# Revit family: 540_Sliding_Window_XOX_Standard
name_source: partatom
category: Windows
revit_build: Autodesk Revit 2014 (Build: 20130308_1515(x64)
units: mm (PartAtom-declared; Revit-internal decimal feet)

## types (96) — shared parameters
Centered In Wall = Yes
Custom Sash Width Middle = 800 mm  [stored 2.62467 ft]
Default Sill Height = 800 mm  [stored 2.62467 ft]
Description = Sliding window, XOX
Equal Sash Width = Yes
Frame Thickness = 54 mm  [stored 0.177165 ft]
Limit Sash Height Max = 1500 mm  [stored 4.92126 ft]
Limit Sash Height Min = 300 mm  [stored 0.984252 ft]
Limit Sash Width Max = 1200 mm  [stored 3.93701 ft]
Limit Sash Width Min = 300 mm  [stored 0.984252 ft]
Limit Window Height Max = 1580 mm
Limit Window Height Min = 380 mm
Limit Window Width Max = 3556 mm
Limit Window Width Min = 856 mm
Manufacturer = Crealco
Model = 540
Sash Frame Seal = 3 mm  [stored 0.00984252 ft]
URL = http://www.crealco.co.za
Wall Closure = By host
zero-valued in all types: Custom Frame Offset From Exterior

## per-type parameters (varying)
| type | Area Middle Sash Glazing | Area Side Sash Glazing | Clearvue SHGC Value | Clearvue U Value | Custom Windload | Custom Window Height | Custom Window Width | Energy Advantage SHGC Value | Heavy Duty Interlocker | Height | Intruderprufe LowE SHGC Value | Intruderprufe LowE U Value | Intruderprufe SHGC Value | Intruderprufe U Value | Is Heavy Duty Mullion | Limit Sash Width Middle Max | Limit Sash Width Middle Min | Max Pane Area | Sash Height | Sash Width Middle | Sash Width Sides | Standard Interlocker | Width | Windload Design |
| 540SW-0906XOX-1000Pa | 0.08 m² | 0.08 m² | 0.327 | 6.76 | 1000 mm  [stored 3.28084 ft] | 590 mm  [stored 1.9357 ft] | 890 mm  [stored 2.91995 ft] | 0.327 | No | 590 mm  [stored 1.9357 ft] | 0.306 | 6.65 | 0.34 | 7.43 | 0 mm  [stored 0 ft] | 334 mm | 300 mm  [stored 0.984252 ft] | 0.08 m² | 510 mm | 311 mm | 311 mm | Yes | 890 mm  [stored 2.91995 ft] | 1000 mm  [stored 3.28084 ft] |
| 540SW-1206XOX-1000Pa | 0.12 m² | 0.12 m² | 0.409 | 7.29 | 1000 mm  [stored 3.28084 ft] | 590 mm  [stored 1.9357 ft] | 1190 mm  [stored 3.9042 ft] | 0.371 | No | 590 mm  [stored 1.9357 ft] | 0.347 | 6.27 | 0.388 | 7.148 | 0 mm  [stored 0 ft] | 634 mm | 300 mm  [stored 0.984252 ft] | 0.12 m² | 510 mm | 411 mm | 411 mm | Yes | 1190 mm  [stored 3.9042 ft] | 1000 mm  [stored 3.28084 ft] |
| 540SW-1506XOX-1000Pa | 0.16 m² | 0.16 m² | 0.44 | 7.15 | 1000 mm  [stored 3.28084 ft] | 590 mm  [stored 1.9357 ft] | 1490 mm  [stored 4.88845 ft] | 0.398 | No | 590 mm  [stored 1.9357 ft] | 0.372 | 6.03 | 0.416 | 7.03 | 0 mm  [stored 0 ft] | 934 mm | 300 mm  [stored 0.984252 ft] | 0.16 m² | 510 mm | 511 mm | 511 mm | Yes | 1490 mm  [stored 4.88845 ft] | 1000 mm  [stored 3.28084 ft] |
| 540SW-1806XOX-1000Pa | 0.2 m² | 0.2 m² | 0.46 | 7.26 | 1000 mm  [stored 3.28084 ft] | 590 mm  [stored 1.9357 ft] | 1790 mm  [stored 5.8727 ft] | 0.415 | No | 590 mm  [stored 1.9357 ft] | 0.389 | 6.01 | 0.435 | 7.1 | 0 mm  [stored 0 ft] | 1200 mm  [stored 3.93701 ft] | 300 mm  [stored 0.984252 ft] | 0.2 m² | 510 mm | 611 mm | 611 mm | Yes | 1790 mm  [stored 5.8727 ft] | 1000 mm  [stored 3.28084 ft] |
| 540SW-2106XOX-1000Pa | 0.24 m² | 0.24 m² | 0.475 | 7.16 | 1000 mm  [stored 3.28084 ft] | 590 mm  [stored 1.9357 ft] | 2090 mm  [stored 6.85696 ft] | 0.428 | No | 590 mm  [stored 1.9357 ft] | 0.4 | 5.88 | 0.449 | 7 | 0 mm  [stored 0 ft] | 1200 mm  [stored 3.93701 ft] | 300 mm  [stored 0.984252 ft] | 0.24 m² | 510 mm | 711 mm | 711 mm | Yes | 2090 mm  [stored 6.85696 ft] | 1000 mm  [stored 3.28084 ft] |
| 540SW-2706XOX-1000Pa | 0.32 m² | 0.32 m² | 0.494 | 7.03 | 1000 mm  [stored 3.28084 ft] | 590 mm  [stored 1.9357 ft] | 2690 mm | 0.445 | No | 590 mm  [stored 1.9357 ft] | 0.416 | 5.71 | 0.467 | 6.88 | 0 mm  [stored 0 ft] | 1200 mm  [stored 3.93701 ft] | 334 mm | 0.32 m² | 510 mm | 911 mm | 911 mm | Yes | 2690 mm | 1000 mm  [stored 3.28084 ft] |
| 540SW-3006XOX-1000Pa | 0.36 m² | 0.36 m² | 0.501 | 6.98 | 1000 mm  [stored 3.28084 ft] | 590 mm  [stored 1.9357 ft] | 2990 mm  [stored 9.80971 ft] | 0.45 | No | 590 mm  [stored 1.9357 ft] | 0.421 | 5.65 | 0.473 | 6.84 | 0 mm  [stored 0 ft] | 1200 mm  [stored 3.93701 ft] | 634 mm | 0.36 m² | 510 mm | 1011 mm | 1011 mm | Yes | 2990 mm  [stored 9.80971 ft] | 1000 mm  [stored 3.28084 ft] |
| 540SW-0909XOX-1000Pa | 0.14 m² | 0.14 m² | 0.417 | 7.52 | 1000 mm  [stored 3.28084 ft] | 890 mm  [stored 2.91995 ft] | 890 mm  [stored 2.91995 ft] | 0.378 | No | 890 mm  [stored 2.91995 ft] | 0.353 | 6.47 | 0.394 | 7.4 | 0 mm  [stored 0 ft] | 334 mm | 300 mm  [stored 0.984252 ft] | 0.14 m² | 810 mm  [stored 2.65748 ft] | 311 mm | 311 mm | Yes | 890 mm  [stored 2.91995 ft] | 1000 mm  [stored 3.28084 ft] |
| 540SW-1209XOX-1000Pa | 0.21 m² | 0.21 m² | 0.477 | 7.22 | 1000 mm  [stored 3.28084 ft] | 890 mm  [stored 2.91995 ft] | 1190 mm  [stored 3.9042 ft] | 0.431 | No | 890 mm  [stored 2.91995 ft] | 0.402 | 6.01 | 0.451 | 7.11 | 0 mm  [stored 0 ft] | 634 mm | 300 mm  [stored 0.984252 ft] | 0.21 m² | 810 mm  [stored 2.65748 ft] | 411 mm | 411 mm | Yes | 1190 mm  [stored 3.9042 ft] | 1000 mm  [stored 3.28084 ft] |
| 540SW-1509XOX-1000Pa | 0.28 m² | 0.28 m² | 0.513 | 7.04 | 1000 mm  [stored 3.28084 ft] | 890 mm  [stored 2.91995 ft] | 1490 mm  [stored 4.88845 ft] | 0.463 | No | 890 mm  [stored 2.91995 ft] | 0.432 | 5.73 | 0.485 | 6.93 | 0 mm  [stored 0 ft] | 934 mm | 300 mm  [stored 0.984252 ft] | 0.28 m² | 810 mm  [stored 2.65748 ft] | 511 mm | 511 mm | Yes | 1490 mm  [stored 4.88845 ft] | 1000 mm  [stored 3.28084 ft] |
| 540SW-1809XOX-1000Pa | 0.35 m² | 0.35 m² | 0.538 | 7.15 | 1000 mm  [stored 3.28084 ft] | 890 mm  [stored 2.91995 ft] | 1790 mm  [stored 5.8727 ft] | 0.483 | No | 890 mm  [stored 2.91995 ft] | 0.452 | 5.68 | 0.508 | 6.98 | 0 mm  [stored 0 ft] | 1200 mm  [stored 3.93701 ft] | 300 mm  [stored 0.984252 ft] | 0.35 m² | 810 mm  [stored 2.65748 ft] | 611 mm | 611 mm | Yes | 1790 mm  [stored 5.8727 ft] | 1000 mm  [stored 3.28084 ft] |
| 540SW-2109XOX-1000Pa | 0.42 m² | 0.42 m² | 0.555 | 7.04 | 1000 mm  [stored 3.28084 ft] | 890 mm  [stored 2.91995 ft] | 2090 mm  [stored 6.85696 ft] | 0.499 | No | 890 mm  [stored 2.91995 ft] | 0.466 | 5.52 | 0.524 | 6.87 | 0 mm  [stored 0 ft] | 1200 mm  [stored 3.93701 ft] | 300 mm  [stored 0.984252 ft] | 0.42 m² | 810 mm  [stored 2.65748 ft] | 711 mm | 711 mm | Yes | 2090 mm  [stored 6.85696 ft] | 1000 mm  [stored 3.28084 ft] |
| 540SW-2409XOX-1000Pa | 0.49 m² | 0.49 m² | 0.568 | 6.95 | 1000 mm  [stored 3.28084 ft] | 890 mm  [stored 2.91995 ft] | 2390 mm  [stored 7.84121 ft] | 0.51 | No | 890 mm  [stored 2.91995 ft] | 0.476 | 5.41 | 0.536 | 6.79 | 0 mm  [stored 0 ft] | 1200 mm  [stored 3.93701 ft] | 300 mm  [stored 0.984252 ft] | 0.49 m² | 810 mm  [stored 2.65748 ft] | 811 mm | 811 mm | Yes | 2390 mm  [stored 7.84121 ft] | 1000 mm  [stored 3.28084 ft] |
| 540SW-2709XOX-1000Pa | 0.56 m² | 0.56 m² | 0.578 | 6.88 | 1000 mm  [stored 3.28084 ft] | 890 mm  [stored 2.91995 ft] | 2690 mm | 0.519 | No | 890 mm  [stored 2.91995 ft] | 0.484 | 5.32 | 0.546 | 6.72 | 0 mm  [stored 0 ft] | 1200 mm  [stored 3.93701 ft] | 334 mm | 0.56 m² | 810 mm  [stored 2.65748 ft] | 911 mm | 911 mm | Yes | 2690 mm | 1000 mm  [stored 3.28084 ft] |
| 540SW-3009XOX-1000Pa | 0.63 m² | 0.63 m² | 0.586 | 6.82 | 1000 mm  [stored 3.28084 ft] | 890 mm  [stored 2.91995 ft] | 2990 mm  [stored 9.80971 ft] | 0.526 | No | 890 mm  [stored 2.91995 ft] | 0.491 | 5.25 | 0.553 | 6.69 | 0 mm  [stored 0 ft] | 1200 mm  [stored 3.93701 ft] | 634 mm | 0.63 m² | 810 mm  [stored 2.65748 ft] | 1011 mm | 1011 mm | Yes | 2990 mm  [stored 9.80971 ft] | 1000 mm  [stored 3.28084 ft] |
| 540SW-0912XOX-1000Pa | 0.2 m² | 0.2 m² | 0.445 | 7.51 | 1000 mm  [stored 3.28084 ft] | 1190 mm  [stored 3.9042 ft] | 890 mm  [stored 2.91995 ft] | 0.403 | No | 1190 mm  [stored 3.9042 ft] | 0.377 | 6.38 | 0.421 | 7.39 | 0 mm  [stored 0 ft] | 334 mm | 300 mm  [stored 0.984252 ft] | 0.2 m² | 1110 mm  [stored 3.64173 ft] | 311 mm | 311 mm | Yes | 890 mm  [stored 2.91995 ft] | 1000 mm  [stored 3.28084 ft] |
| 540SW-1212XOX-1000Pa | 0.3 m² | 0.3 m² | 0.511 | 7.19 | 1000 mm  [stored 3.28084 ft] | 1190 mm  [stored 3.9042 ft] | 1190 mm  [stored 3.9042 ft] | 0.461 | No | 1190 mm  [stored 3.9042 ft] | 0.43 | 5.88 | 0.482 | 7.07 | 0 mm  [stored 0 ft] | 634 mm | 300 mm  [stored 0.984252 ft] | 0.3 m² | 1110 mm  [stored 3.64173 ft] | 411 mm | 411 mm | Yes | 1190 mm  [stored 3.9042 ft] | 1000 mm  [stored 3.28084 ft] |
| 540SW-1512XOX-1000Pa | 0.4 m² | 0.4 m² | 0.55 | 6.99 | 1000 mm  [stored 3.28084 ft] | 1190 mm  [stored 3.9042 ft] | 1490 mm  [stored 4.88845 ft] | 0.495 | No | 1190 mm  [stored 3.9042 ft] | 0.462 | 5.57 | 0.519 | 6.87 | 0 mm  [stored 0 ft] | 934 mm | 300 mm  [stored 0.984252 ft] | 0.4 m² | 1110 mm  [stored 3.64173 ft] | 511 mm | 511 mm | Yes | 1490 mm  [stored 4.88845 ft] | 1000 mm  [stored 3.28084 ft] |
| 540SW-1812XOX-1000Pa | 0.5 m² | 0.5 m² | 0.576 | 7.1 | 1000 mm  [stored 3.28084 ft] | 1190 mm  [stored 3.9042 ft] | 1790 mm  [stored 5.8727 ft] | 0.517 | No | 1190 mm  [stored 3.9042 ft] | 0.483 | 5.52 | 0.544 | 6.92 | 0 mm  [stored 0 ft] | 1200 mm  [stored 3.93701 ft] | 300 mm  [stored 0.984252 ft] | 0.5 m² | 1110 mm  [stored 3.64173 ft] | 611 mm | 611 mm | Yes | 1790 mm  [stored 5.8727 ft] | 1000 mm  [stored 3.28084 ft] |
| 540SW-2112XOX-1000Pa | 0.6 m² | 0.6 m² | 0.595 | 6.98 | 1000 mm  [stored 3.28084 ft] | 1190 mm  [stored 3.9042 ft] | 2090 mm  [stored 6.85696 ft] | 0.534 | No | 1190 mm  [stored 3.9042 ft] | 0.498 | 5.35 | 0.561 | 6.8 | 0 mm  [stored 0 ft] | 1200 mm  [stored 3.93701 ft] | 300 mm  [stored 0.984252 ft] | 0.6 m² | 1110 mm  [stored 3.64173 ft] | 711 mm | 711 mm | Yes | 2090 mm  [stored 6.85696 ft] | 1000 mm  [stored 3.28084 ft] |
| 540SW-2412XOX-1000Pa | 0.71 m² | 0.71 m² | 0.609 | 6.88 | 1000 mm  [stored 3.28084 ft] | 1190 mm  [stored 3.9042 ft] | 2390 mm  [stored 7.84121 ft] | 0.546 | No | 1190 mm  [stored 3.9042 ft] | 0.51 | 5.23 | 0.575 | 6.72 | 0 mm  [stored 0 ft] | 1200 mm  [stored 3.93701 ft] | 300 mm  [stored 0.984252 ft] | 0.71 m² | 1110 mm  [stored 3.64173 ft] | 811 mm | 811 mm | Yes | 2390 mm  [stored 7.84121 ft] | 1000 mm  [stored 3.28084 ft] |
| 540SW-2712XOX-1000Pa | 0.81 m² | 0.81 m² | 0.62 | 6.81 | 1000 mm  [stored 3.28084 ft] | 1190 mm  [stored 3.9042 ft] | 2690 mm | 0.556 | No | 1190 mm  [stored 3.9042 ft] | 0.518 | 5.13 | 0.585 | 6.65 | 0 mm  [stored 0 ft] | 1200 mm  [stored 3.93701 ft] | 334 mm | 0.81 m² | 1110 mm  [stored 3.64173 ft] | 911 mm | 911 mm | Yes | 2690 mm | 1000 mm  [stored 3.28084 ft] |
| 540SW-3012XOX-1000Pa | 0.91 m² | 0.91 m² | 0.629 | 6.75 | 1000 mm  [stored 3.28084 ft] | 1190 mm  [stored 3.9042 ft] | 2990 mm  [stored 9.80971 ft] | 0.563 | No | 1190 mm  [stored 3.9042 ft] | 0.525 | 5.05 | 0.593 | 6.59 | 0 mm  [stored 0 ft] | 1200 mm  [stored 3.93701 ft] | 634 mm | 0.91 m² | 1110 mm  [stored 3.64173 ft] | 1011 mm | 1011 mm | Yes | 2990 mm  [stored 9.80971 ft] | 1000 mm  [stored 3.28084 ft] |
| 540SW-0915XOX-1000Pa | 0.26 m² | 0.26 m² | 0.462 | 7.5 | 1000 mm  [stored 3.28084 ft] | 1490 mm  [stored 4.88845 ft] | 890 mm  [stored 2.91995 ft] | 0.419 | No | 1490 mm  [stored 4.88845 ft] | 0.391 | 6.33 | 0.437 | 7.38 | 0 mm  [stored 0 ft] | 334 mm | 300 mm  [stored 0.984252 ft] | 0.26 m² | 1410 mm | 311 mm | 311 mm | Yes | 890 mm  [stored 2.91995 ft] | 1000 mm  [stored 3.28084 ft] |
| 540SW-1215XOX-1000Pa | 0.4 m² | 0.4 m² | 0.531 | 7.17 | 1000 mm  [stored 3.28084 ft] | 1490 mm  [stored 4.88845 ft] | 1190 mm  [stored 3.9042 ft] | 0.478 | No | 1490 mm  [stored 4.88845 ft] | 0.446 | 5.8 | 0.501 | 7.05 | 0 mm  [stored 0 ft] | 634 mm | 300 mm  [stored 0.984252 ft] | 0.4 m² | 1410 mm | 411 mm | 411 mm | Yes | 1190 mm  [stored 3.9042 ft] | 1000 mm  [stored 3.28084 ft] |
| 540SW-1515XOX-1000Pa | 0.53 m² | 0.53 m² | 0.572 | 7.26 | 1000 mm  [stored 3.28084 ft] | 1490 mm  [stored 4.88845 ft] | 1490 mm  [stored 4.88845 ft] | 0.513 | No | 1490 mm  [stored 4.88845 ft] | 0.479 | 5.66 | 0.54 | 7.06 | 0 mm  [stored 0 ft] | 934 mm | 300 mm  [stored 0.984252 ft] | 0.53 m² | 1410 mm | 511 mm | 511 mm | Yes | 1490 mm  [stored 4.88845 ft] | 1000 mm  [stored 3.28084 ft] |
| 540SW-1815XOX-1000Pa | 0.66 m² | 0.66 m² | 0.599 | 7.07 | 1000 mm  [stored 3.28084 ft] | 1490 mm  [stored 4.88845 ft] | 1790 mm  [stored 5.8727 ft] | 0.538 | No | 1490 mm  [stored 4.88845 ft] | 0.502 | 5.42 | 0.565 | 6.89 | 0 mm  [stored 0 ft] | 1200 mm  [stored 3.93701 ft] | 300 mm  [stored 0.984252 ft] | 0.66 m² | 1410 mm | 611 mm | 611 mm | Yes | 1790 mm  [stored 5.8727 ft] | 1000 mm  [stored 3.28084 ft] |
| 540SW-2115XOX-1000Pa | 0.79 m² | 0.79 m² | 0.619 | 6.94 | 1000 mm  [stored 3.28084 ft] | 1490 mm  [stored 4.88845 ft] | 2090 mm  [stored 6.85696 ft] | 0.555 | Yes | 1490 mm  [stored 4.88845 ft] | 0.518 | 5.24 | 0.584 | 6.76 | 1 mm  [stored 0.00328084 ft] | 1200 mm  [stored 3.93701 ft] | 300 mm  [stored 0.984252 ft] | 0.79 m² | 1410 mm | 711 mm | 711 mm | No | 2090 mm  [stored 6.85696 ft] | 1000 mm  [stored 3.28084 ft] |
| 540SW-2415XOX-1000Pa | 0.92 m² | 0.92 m² | 0.633 | 6.84 | 1000 mm  [stored 3.28084 ft] | 1490 mm  [stored 4.88845 ft] | 2390 mm  [stored 7.84121 ft] | 0.568 | Yes | 1490 mm  [stored 4.88845 ft] | 0.529 | 5.12 | 0.597 | 6.67 | 1 mm  [stored 0.00328084 ft] | 1200 mm  [stored 3.93701 ft] | 300 mm  [stored 0.984252 ft] | 0.92 m² | 1410 mm | 811 mm | 811 mm | No | 2390 mm  [stored 7.84121 ft] | 1000 mm  [stored 3.28084 ft] |
| 540SW-2715XOX-1000Pa | 1.05 m² | 1.05 m² | 0.645 | 6.76 | 1000 mm  [stored 3.28084 ft] | 1490 mm  [stored 4.88845 ft] | 2690 mm | 0.578 | Yes | 1490 mm  [stored 4.88845 ft] | 0.539 | 5.02 | 0.608 | 6.6 | 1 mm  [stored 0.00328084 ft] | 1200 mm  [stored 3.93701 ft] | 334 mm | 1.05 m² | 1410 mm | 911 mm | 911 mm | No | 2690 mm | 1000 mm  [stored 3.28084 ft] |
| 540SW-3015XOX-1000Pa | 1.18 m² | 1.18 m² | 0.654 | 6.7 | 1000 mm  [stored 3.28084 ft] | 1490 mm  [stored 4.88845 ft] | 2990 mm  [stored 9.80971 ft] | 0.586 | Yes | 1490 mm  [stored 4.88845 ft] | 0.546 | 4.93 | 0.617 | 6.54 | 1 mm  [stored 0.00328084 ft] | 1200 mm  [stored 3.93701 ft] | 634 mm | 1.18 m² | 1410 mm | 1011 mm | 1011 mm | No | 2990 mm  [stored 9.80971 ft] | 1000 mm  [stored 3.28084 ft] |
| 540SW-2406XOX-1000Pa | 0.28 m² | 0.28 m² | 0.486 | 7.08 | 1000 mm  [stored 3.28084 ft] | 590 mm  [stored 1.9357 ft] | 2390 mm  [stored 7.84121 ft] | 0.437 | No | 590 mm  [stored 1.9357 ft] | 0.409 | 5.78 | 0.459 | 6.93 | 0 mm  [stored 0 ft] | 1200 mm  [stored 3.93701 ft] | 300 mm  [stored 0.984252 ft] | 0.28 m² | 510 mm | 811 mm | 811 mm | Yes | 2390 mm  [stored 7.84121 ft] | 1000 mm  [stored 3.28084 ft] |
| 540SW-0906XOX-1500Pa | 0.08 m² | 0.08 m² | 0.327 | 6.76 | 1500 mm  [stored 4.92126 ft] | 590 mm  [stored 1.9357 ft] | 890 mm  [stored 2.91995 ft] | 0.327 | No | 590 mm  [stored 1.9357 ft] | 0.306 | 6.65 | 0.34 | 7.43 | 0 mm  [stored 0 ft] | 334 mm | 300 mm  [stored 0.984252 ft] | 0.08 m² | 510 mm | 311 mm | 311 mm | Yes | 890 mm  [stored 2.91995 ft] | 1500 mm  [stored 4.92126 ft] |
| 540SW-0906XOX-2000Pa | 0.08 m² | 0.08 m² | 0.327 | 6.76 | 2000 mm  [stored 6.56168 ft] | 590 mm  [stored 1.9357 ft] | 890 mm  [stored 2.91995 ft] | 0.327 | No | 590 mm  [stored 1.9357 ft] | 0.306 | 6.65 | 0.34 | 7.43 | 0 mm  [stored 0 ft] | 334 mm | 300 mm  [stored 0.984252 ft] | 0.08 m² | 510 mm | 311 mm | 311 mm | Yes | 890 mm  [stored 2.91995 ft] | 2000 mm  [stored 6.56168 ft] |
| 540SW-0909XOX-1500Pa | 0.14 m² | 0.14 m² | 0.417 | 7.52 | 1500 mm  [stored 4.92126 ft] | 890 mm  [stored 2.91995 ft] | 890 mm  [stored 2.91995 ft] | 0.378 | No | 890 mm  [stored 2.91995 ft] | 0.353 | 6.47 | 0.394 | 7.4 | 0 mm  [stored 0 ft] | 334 mm | 300 mm  [stored 0.984252 ft] | 0.14 m² | 810 mm  [stored 2.65748 ft] | 311 mm | 311 mm | Yes | 890 mm  [stored 2.91995 ft] | 1500 mm  [stored 4.92126 ft] |
| 540SW-0909XOX-2000Pa | 0.14 m² | 0.14 m² | 0.417 | 7.52 | 2000 mm  [stored 6.56168 ft] | 890 mm  [stored 2.91995 ft] | 890 mm  [stored 2.91995 ft] | 0.378 | No | 890 mm  [stored 2.91995 ft] | 0.353 | 6.47 | 0.394 | 7.4 | 0 mm  [stored 0 ft] | 334 mm | 300 mm  [stored 0.984252 ft] | 0.14 m² | 810 mm  [stored 2.65748 ft] | 311 mm | 311 mm | Yes | 890 mm  [stored 2.91995 ft] | 2000 mm  [stored 6.56168 ft] |
| 540SW-0912XOX-1500Pa | 0.2 m² | 0.2 m² | 0.445 | 7.51 | 1500 mm  [stored 4.92126 ft] | 1190 mm  [stored 3.9042 ft] | 890 mm  [stored 2.91995 ft] | 0.403 | No | 1190 mm  [stored 3.9042 ft] | 0.377 | 6.38 | 0.421 | 7.39 | 0 mm  [stored 0 ft] | 334 mm | 300 mm  [stored 0.984252 ft] | 0.2 m² | 1110 mm  [stored 3.64173 ft] | 311 mm | 311 mm | Yes | 890 mm  [stored 2.91995 ft] | 1500 mm  [stored 4.92126 ft] |
| 540SW-0912XOX-2000Pa | 0.2 m² | 0.2 m² | 0.445 | 7.51 | 2000 mm  [stored 6.56168 ft] | 1190 mm  [stored 3.9042 ft] | 890 mm  [stored 2.91995 ft] | 0.403 | No | 1190 mm  [stored 3.9042 ft] | 0.377 | 6.38 | 0.421 | 7.39 | 0 mm  [stored 0 ft] | 334 mm | 300 mm  [stored 0.984252 ft] | 0.2 m² | 1110 mm  [stored 3.64173 ft] | 311 mm | 311 mm | Yes | 890 mm  [stored 2.91995 ft] | 2000 mm  [stored 6.56168 ft] |
| 540SW-0915XOX-1500Pa | 0.26 m² | 0.26 m² | 0.462 | 7.5 | 1500 mm  [stored 4.92126 ft] | 1490 mm  [stored 4.88845 ft] | 890 mm  [stored 2.91995 ft] | 0.419 | No | 1490 mm  [stored 4.88845 ft] | 0.391 | 6.33 | 0.437 | 7.38 | 0 mm  [stored 0 ft] | 334 mm | 300 mm  [stored 0.984252 ft] | 0.26 m² | 1410 mm | 311 mm | 311 mm | Yes | 890 mm  [stored 2.91995 ft] | 1500 mm  [stored 4.92126 ft] |
| 540SW-0915XOX-2000Pa | 0.26 m² | 0.26 m² | 0.462 | 7.5 | 2000 mm  [stored 6.56168 ft] | 1490 mm  [stored 4.88845 ft] | 890 mm  [stored 2.91995 ft] | 0.419 | No | 1490 mm  [stored 4.88845 ft] | 0.391 | 6.33 | 0.437 | 7.38 | 0 mm  [stored 0 ft] | 334 mm | 300 mm  [stored 0.984252 ft] | 0.26 m² | 1410 mm | 311 mm | 311 mm | Yes | 890 mm  [stored 2.91995 ft] | 2000 mm  [stored 6.56168 ft] |
| 540SW-1206XOX-1500Pa | 0.12 m² | 0.12 m² | 0.409 | 7.29 | 1500 mm  [stored 4.92126 ft] | 590 mm  [stored 1.9357 ft] | 1190 mm  [stored 3.9042 ft] | 0.371 | No | 590 mm  [stored 1.9357 ft] | 0.347 | 6.27 | 0.388 | 7.148 | 0 mm  [stored 0 ft] | 634 mm | 300 mm  [stored 0.984252 ft] | 0.12 m² | 510 mm | 411 mm | 411 mm | Yes | 1190 mm  [stored 3.9042 ft] | 1500 mm  [stored 4.92126 ft] |
| 540SW-1206XOX-2000Pa | 0.12 m² | 0.12 m² | 0.409 | 7.29 | 1500 mm  [stored 4.92126 ft] | 590 mm  [stored 1.9357 ft] | 1190 mm  [stored 3.9042 ft] | 0.371 | No | 590 mm  [stored 1.9357 ft] | 0.347 | 6.27 | 0.388 | 7.148 | 0 mm  [stored 0 ft] | 634 mm | 300 mm  [stored 0.984252 ft] | 0.12 m² | 510 mm | 411 mm | 411 mm | Yes | 1190 mm  [stored 3.9042 ft] | 1500 mm  [stored 4.92126 ft] |
| 540SW-1209XOX-1500Pa | 0.21 m² | 0.21 m² | 0.477 | 7.22 | 1500 mm  [stored 4.92126 ft] | 890 mm  [stored 2.91995 ft] | 1190 mm  [stored 3.9042 ft] | 0.431 | No | 890 mm  [stored 2.91995 ft] | 0.402 | 6.01 | 0.451 | 7.11 | 0 mm  [stored 0 ft] | 634 mm | 300 mm  [stored 0.984252 ft] | 0.21 m² | 810 mm  [stored 2.65748 ft] | 411 mm | 411 mm | Yes | 1190 mm  [stored 3.9042 ft] | 1500 mm  [stored 4.92126 ft] |
| 540SW-1209XOX-2000Pa | 0.21 m² | 0.21 m² | 0.477 | 7.22 | 2000 mm  [stored 6.56168 ft] | 890 mm  [stored 2.91995 ft] | 1190 mm  [stored 3.9042 ft] | 0.431 | No | 890 mm  [stored 2.91995 ft] | 0.402 | 6.01 | 0.451 | 7.11 | 0 mm  [stored 0 ft] | 634 mm | 300 mm  [stored 0.984252 ft] | 0.21 m² | 810 mm  [stored 2.65748 ft] | 411 mm | 411 mm | Yes | 1190 mm  [stored 3.9042 ft] | 2000 mm  [stored 6.56168 ft] |
| 540SW-1212XOX-1500Pa | 0.3 m² | 0.3 m² | 0.511 | 7.19 | 1500 mm  [stored 4.92126 ft] | 1190 mm  [stored 3.9042 ft] | 1190 mm  [stored 3.9042 ft] | 0.461 | No | 1190 mm  [stored 3.9042 ft] | 0.43 | 5.88 | 0.482 | 7.07 | 0 mm  [stored 0 ft] | 634 mm | 300 mm  [stored 0.984252 ft] | 0.3 m² | 1110 mm  [stored 3.64173 ft] | 411 mm | 411 mm | Yes | 1190 mm  [stored 3.9042 ft] | 1500 mm  [stored 4.92126 ft] |
| 540SW-1212XOX-2000Pa | 0.3 m² | 0.3 m² | 0.511 | 7.19 | 2000 mm  [stored 6.56168 ft] | 1190 mm  [stored 3.9042 ft] | 1190 mm  [stored 3.9042 ft] | 0.461 | No | 1190 mm  [stored 3.9042 ft] | 0.43 | 5.88 | 0.482 | 7.07 | 0 mm  [stored 0 ft] | 634 mm | 300 mm  [stored 0.984252 ft] | 0.3 m² | 1110 mm  [stored 3.64173 ft] | 411 mm | 411 mm | Yes | 1190 mm  [stored 3.9042 ft] | 2000 mm  [stored 6.56168 ft] |
| 540SW-1215XOX-1500Pa | 0.4 m² | 0.4 m² | 0.531 | 7.17 | 1500 mm  [stored 4.92126 ft] | 1490 mm  [stored 4.88845 ft] | 1190 mm  [stored 3.9042 ft] | 0.478 | No | 1490 mm  [stored 4.88845 ft] | 0.446 | 5.8 | 0.501 | 7.05 | 0 mm  [stored 0 ft] | 634 mm | 300 mm  [stored 0.984252 ft] | 0.4 m² | 1410 mm | 411 mm | 411 mm | Yes | 1190 mm  [stored 3.9042 ft] | 1500 mm  [stored 4.92126 ft] |
| 540SW-1215XOX-2000Pa | 0.4 m² | 0.4 m² | 0.531 | 7.17 | 2000 mm  [stored 6.56168 ft] | 1490 mm  [stored 4.88845 ft] | 1190 mm  [stored 3.9042 ft] | 0.478 | Yes | 1490 mm  [stored 4.88845 ft] | 0.446 | 5.8 | 0.501 | 7.05 | 1 mm  [stored 0.00328084 ft] | 634 mm | 300 mm  [stored 0.984252 ft] | 0.4 m² | 1410 mm | 411 mm | 411 mm | No | 1190 mm  [stored 3.9042 ft] | 2000 mm  [stored 6.56168 ft] |
| 540SW-1506XOX-1500Pa | 0.16 m² | 0.16 m² | 0.44 | 7.15 | 1500 mm  [stored 4.92126 ft] | 590 mm  [stored 1.9357 ft] | 1490 mm  [stored 4.88845 ft] | 0.398 | No | 590 mm  [stored 1.9357 ft] | 0.372 | 6.03 | 0.416 | 7.03 | 0 mm  [stored 0 ft] | 934 mm | 300 mm  [stored 0.984252 ft] | 0.16 m² | 510 mm | 511 mm | 511 mm | Yes | 1490 mm  [stored 4.88845 ft] | 1500 mm  [stored 4.92126 ft] |
| 540SW-1506XOX-2000Pa | 0.16 m² | 0.16 m² | 0.44 | 7.15 | 2000 mm  [stored 6.56168 ft] | 590 mm  [stored 1.9357 ft] | 1490 mm  [stored 4.88845 ft] | 0.398 | No | 590 mm  [stored 1.9357 ft] | 0.372 | 6.03 | 0.416 | 7.03 | 0 mm  [stored 0 ft] | 934 mm | 300 mm  [stored 0.984252 ft] | 0.16 m² | 510 mm | 511 mm | 511 mm | Yes | 1490 mm  [stored 4.88845 ft] | 2000 mm  [stored 6.56168 ft] |
| 540SW-1509XOX-1500Pa | 0.28 m² | 0.28 m² | 0.513 | 7.04 | 1500 mm  [stored 4.92126 ft] | 890 mm  [stored 2.91995 ft] | 1490 mm  [stored 4.88845 ft] | 0.463 | No | 890 mm  [stored 2.91995 ft] | 0.432 | 5.73 | 0.485 | 6.93 | 0 mm  [stored 0 ft] | 934 mm | 300 mm  [stored 0.984252 ft] | 0.28 m² | 810 mm  [stored 2.65748 ft] | 511 mm | 511 mm | Yes | 1490 mm  [stored 4.88845 ft] | 1500 mm  [stored 4.92126 ft] |
| 540SW-1509XOX-2000Pa | 0.28 m² | 0.28 m² | 0.513 | 7.04 | 2000 mm  [stored 6.56168 ft] | 890 mm  [stored 2.91995 ft] | 1490 mm  [stored 4.88845 ft] | 0.463 | No | 890 mm  [stored 2.91995 ft] | 0.432 | 5.73 | 0.485 | 6.93 | 0 mm  [stored 0 ft] | 934 mm | 300 mm  [stored 0.984252 ft] | 0.28 m² | 810 mm  [stored 2.65748 ft] | 511 mm | 511 mm | Yes | 1490 mm  [stored 4.88845 ft] | 2000 mm  [stored 6.56168 ft] |
| 540SW-1512XOX-1500Pa | 0.4 m² | 0.4 m² | 0.55 | 6.99 | 1500 mm  [stored 4.92126 ft] | 1190 mm  [stored 3.9042 ft] | 1490 mm  [stored 4.88845 ft] | 0.495 | No | 1190 mm  [stored 3.9042 ft] | 0.462 | 5.57 | 0.519 | 6.87 | 0 mm  [stored 0 ft] | 934 mm | 300 mm  [stored 0.984252 ft] | 0.4 m² | 1110 mm  [stored 3.64173 ft] | 511 mm | 511 mm | Yes | 1490 mm  [stored 4.88845 ft] | 1500 mm  [stored 4.92126 ft] |
| 540SW-1512XOX-2000Pa | 0.4 m² | 0.4 m² | 0.55 | 6.99 | 2000 mm  [stored 6.56168 ft] | 1190 mm  [stored 3.9042 ft] | 1490 mm  [stored 4.88845 ft] | 0.495 | No | 1190 mm  [stored 3.9042 ft] | 0.462 | 5.57 | 0.519 | 6.87 | 0 mm  [stored 0 ft] | 934 mm | 300 mm  [stored 0.984252 ft] | 0.4 m² | 1110 mm  [stored 3.64173 ft] | 511 mm | 511 mm | Yes | 1490 mm  [stored 4.88845 ft] | 2000 mm  [stored 6.56168 ft] |
| 540SW-1515XOX-1500Pa | 0.53 m² | 0.53 m² | 0.572 | 7.26 | 1500 mm  [stored 4.92126 ft] | 1490 mm  [stored 4.88845 ft] | 1490 mm  [stored 4.88845 ft] | 0.513 | Yes | 1490 mm  [stored 4.88845 ft] | 0.479 | 5.66 | 0.54 | 7.06 | 1 mm  [stored 0.00328084 ft] | 934 mm | 300 mm  [stored 0.984252 ft] | 0.53 m² | 1410 mm | 511 mm | 511 mm | No | 1490 mm  [stored 4.88845 ft] | 1500 mm  [stored 4.92126 ft] |
| 540SW-1515XOX-2000Pa | 0.53 m² | 0.53 m² | 0.572 | 7.26 | 2000 mm  [stored 6.56168 ft] | 1490 mm  [stored 4.88845 ft] | 1490 mm  [stored 4.88845 ft] | 0.513 | Yes | 1490 mm  [stored 4.88845 ft] | 0.479 | 5.66 | 0.54 | 7.06 | 1 mm  [stored 0.00328084 ft] | 934 mm | 300 mm  [stored 0.984252 ft] | 0.53 m² | 1410 mm | 511 mm | 511 mm | No | 1490 mm  [stored 4.88845 ft] | 2000 mm  [stored 6.56168 ft] |
| 540SW-1806XOX-1500Pa | 0.2 m² | 0.2 m² | 0.46 | 7.26 | 1500 mm  [stored 4.92126 ft] | 590 mm  [stored 1.9357 ft] | 1790 mm  [stored 5.8727 ft] | 0.415 | No | 590 mm  [stored 1.9357 ft] | 0.389 | 6.01 | 0.435 | 7.1 | 0 mm  [stored 0 ft] | 1200 mm  [stored 3.93701 ft] | 300 mm  [stored 0.984252 ft] | 0.2 m² | 510 mm | 611 mm | 611 mm | Yes | 1790 mm  [stored 5.8727 ft] | 1500 mm  [stored 4.92126 ft] |
| 540SW-1806XOX-2000Pa | 0.2 m² | 0.2 m² | 0.46 | 7.26 | 2000 mm  [stored 6.56168 ft] | 590 mm  [stored 1.9357 ft] | 1790 mm  [stored 5.8727 ft] | 0.415 | No | 590 mm  [stored 1.9357 ft] | 0.389 | 6.01 | 0.435 | 7.1 | 0 mm  [stored 0 ft] | 1200 mm  [stored 3.93701 ft] | 300 mm  [stored 0.984252 ft] | 0.2 m² | 510 mm | 611 mm | 611 mm | Yes | 1790 mm  [stored 5.8727 ft] | 2000 mm  [stored 6.56168 ft] |
| 540SW-1809XOX-1500Pa | 0.35 m² | 0.35 m² | 0.538 | 7.15 | 1500 mm  [stored 4.92126 ft] | 890 mm  [stored 2.91995 ft] | 1790 mm  [stored 5.8727 ft] | 0.483 | No | 890 mm  [stored 2.91995 ft] | 0.452 | 5.68 | 0.508 | 6.98 | 0 mm  [stored 0 ft] | 1200 mm  [stored 3.93701 ft] | 300 mm  [stored 0.984252 ft] | 0.35 m² | 810 mm  [stored 2.65748 ft] | 611 mm | 611 mm | Yes | 1790 mm  [stored 5.8727 ft] | 1500 mm  [stored 4.92126 ft] |
| 540SW-1809XOX-2000Pa | 0.35 m² | 0.35 m² | 0.538 | 7.15 | 2000 mm  [stored 6.56168 ft] | 890 mm  [stored 2.91995 ft] | 1790 mm  [stored 5.8727 ft] | 0.483 | No | 890 mm  [stored 2.91995 ft] | 0.452 | 5.68 | 0.508 | 6.98 | 0 mm  [stored 0 ft] | 1200 mm  [stored 3.93701 ft] | 300 mm  [stored 0.984252 ft] | 0.35 m² | 810 mm  [stored 2.65748 ft] | 611 mm | 611 mm | Yes | 1790 mm  [stored 5.8727 ft] | 2000 mm  [stored 6.56168 ft] |
| 540SW-1812XOX-1500Pa | 0.5 m² | 0.5 m² | 0.576 | 7.1 | 1500 mm  [stored 4.92126 ft] | 1190 mm  [stored 3.9042 ft] | 1790 mm  [stored 5.8727 ft] | 0.517 | No | 1190 mm  [stored 3.9042 ft] | 0.483 | 5.52 | 0.544 | 6.92 | 0 mm  [stored 0 ft] | 1200 mm  [stored 3.93701 ft] | 300 mm  [stored 0.984252 ft] | 0.5 m² | 1110 mm  [stored 3.64173 ft] | 611 mm | 611 mm | Yes | 1790 mm  [stored 5.8727 ft] | 1500 mm  [stored 4.92126 ft] |
| 540SW-1812XOX-2000Pa | 0.5 m² | 0.5 m² | 0.576 | 7.1 | 2000 mm  [stored 6.56168 ft] | 1190 mm  [stored 3.9042 ft] | 1790 mm  [stored 5.8727 ft] | 0.517 | No | 1190 mm  [stored 3.9042 ft] | 0.483 | 5.52 | 0.544 | 6.92 | 0 mm  [stored 0 ft] | 1200 mm  [stored 3.93701 ft] | 300 mm  [stored 0.984252 ft] | 0.5 m² | 1110 mm  [stored 3.64173 ft] | 611 mm | 611 mm | Yes | 1790 mm  [stored 5.8727 ft] | 2000 mm  [stored 6.56168 ft] |
| 540SW-1815XOX-1500Pa | 0.66 m² | 0.66 m² | 0.599 | 7.07 | 1500 mm  [stored 4.92126 ft] | 1490 mm  [stored 4.88845 ft] | 1790 mm  [stored 5.8727 ft] | 0.538 | Yes | 1490 mm  [stored 4.88845 ft] | 0.502 | 5.42 | 0.565 | 6.89 | 1 mm  [stored 0.00328084 ft] | 1200 mm  [stored 3.93701 ft] | 300 mm  [stored 0.984252 ft] | 0.66 m² | 1410 mm | 611 mm | 611 mm | No | 1790 mm  [stored 5.8727 ft] | 1500 mm  [stored 4.92126 ft] |
| 540SW-1815XOX-2000Pa | 0.66 m² | 0.66 m² | 0.599 | 7.07 | 2000 mm  [stored 6.56168 ft] | 1490 mm  [stored 4.88845 ft] | 1790 mm  [stored 5.8727 ft] | 0.538 | Yes | 1490 mm  [stored 4.88845 ft] | 0.502 | 5.42 | 0.565 | 6.89 | 1 mm  [stored 0.00328084 ft] | 1200 mm  [stored 3.93701 ft] | 300 mm  [stored 0.984252 ft] | 0.66 m² | 1410 mm | 611 mm | 611 mm | No | 1790 mm  [stored 5.8727 ft] | 2000 mm  [stored 6.56168 ft] |
| 540SW-2106XOX-1500Pa | 0.24 m² | 0.24 m² | 0.475 | 7.16 | 1500 mm  [stored 4.92126 ft] | 590 mm  [stored 1.9357 ft] | 2090 mm  [stored 6.85696 ft] | 0.428 | No | 590 mm  [stored 1.9357 ft] | 0.4 | 5.88 | 0.449 | 7 | 0 mm  [stored 0 ft] | 1200 mm  [stored 3.93701 ft] | 300 mm  [stored 0.984252 ft] | 0.24 m² | 510 mm | 711 mm | 711 mm | Yes | 2090 mm  [stored 6.85696 ft] | 1500 mm  [stored 4.92126 ft] |
| 540SW-2106XOX-2000Pa | 0.24 m² | 0.24 m² | 0.475 | 7.16 | 2000 mm  [stored 6.56168 ft] | 590 mm  [stored 1.9357 ft] | 2090 mm  [stored 6.85696 ft] | 0.428 | No | 590 mm  [stored 1.9357 ft] | 0.4 | 5.88 | 0.449 | 7 | 0 mm  [stored 0 ft] | 1200 mm  [stored 3.93701 ft] | 300 mm  [stored 0.984252 ft] | 0.24 m² | 510 mm | 711 mm | 711 mm | Yes | 2090 mm  [stored 6.85696 ft] | 2000 mm  [stored 6.56168 ft] |
| 540SW-2109XOX-1500Pa | 0.42 m² | 0.42 m² | 0.555 | 7.04 | 1500 mm  [stored 4.92126 ft] | 890 mm  [stored 2.91995 ft] | 2090 mm  [stored 6.85696 ft] | 0.499 | No | 890 mm  [stored 2.91995 ft] | 0.466 | 5.52 | 0.524 | 6.87 | 0 mm  [stored 0 ft] | 1200 mm  [stored 3.93701 ft] | 300 mm  [stored 0.984252 ft] | 0.42 m² | 810 mm  [stored 2.65748 ft] | 711 mm | 711 mm | Yes | 2090 mm  [stored 6.85696 ft] | 1500 mm  [stored 4.92126 ft] |
| 540SW-2109XOX-2000Pa | 0.42 m² | 0.42 m² | 0.555 | 7.04 | 2000 mm  [stored 6.56168 ft] | 890 mm  [stored 2.91995 ft] | 2090 mm  [stored 6.85696 ft] | 0.499 | No | 890 mm  [stored 2.91995 ft] | 0.466 | 5.52 | 0.524 | 6.87 | 0 mm  [stored 0 ft] | 1200 mm  [stored 3.93701 ft] | 300 mm  [stored 0.984252 ft] | 0.42 m² | 810 mm  [stored 2.65748 ft] | 711 mm | 711 mm | Yes | 2090 mm  [stored 6.85696 ft] | 2000 mm  [stored 6.56168 ft] |
| 540SW-2112XOX-1500Pa | 0.6 m² | 0.6 m² | 0.595 | 6.98 | 1500 mm  [stored 4.92126 ft] | 1190 mm  [stored 3.9042 ft] | 2090 mm  [stored 6.85696 ft] | 0.534 | No | 1190 mm  [stored 3.9042 ft] | 0.498 | 5.35 | 0.561 | 6.8 | 0 mm  [stored 0 ft] | 1200 mm  [stored 3.93701 ft] | 300 mm  [stored 0.984252 ft] | 0.6 m² | 1110 mm  [stored 3.64173 ft] | 711 mm | 711 mm | Yes | 2090 mm  [stored 6.85696 ft] | 1500 mm  [stored 4.92126 ft] |
| 540SW-2112XOX-2000Pa | 0.6 m² | 0.6 m² | 0.595 | 6.98 | 2000 mm  [stored 6.56168 ft] | 1190 mm  [stored 3.9042 ft] | 2090 mm  [stored 6.85696 ft] | 0.534 | No | 1190 mm  [stored 3.9042 ft] | 0.498 | 5.35 | 0.561 | 6.8 | 0 mm  [stored 0 ft] | 1200 mm  [stored 3.93701 ft] | 300 mm  [stored 0.984252 ft] | 0.6 m² | 1110 mm  [stored 3.64173 ft] | 711 mm | 711 mm | Yes | 2090 mm  [stored 6.85696 ft] | 2000 mm  [stored 6.56168 ft] |
| 540SW-2115XOX-1500Pa | 0.79 m² | 0.79 m² | 0.619 | 6.94 | 1500 mm  [stored 4.92126 ft] | 1490 mm  [stored 4.88845 ft] | 2090 mm  [stored 6.85696 ft] | 0.555 | Yes | 1490 mm  [stored 4.88845 ft] | 0.518 | 5.24 | 0.584 | 6.76 | 1 mm  [stored 0.00328084 ft] | 1200 mm  [stored 3.93701 ft] | 300 mm  [stored 0.984252 ft] | 0.79 m² | 1410 mm | 711 mm | 711 mm | No | 2090 mm  [stored 6.85696 ft] | 1500 mm  [stored 4.92126 ft] |
| 540SW-2115XOX-2000Pa | 0.79 m² | 0.79 m² | 0.619 | 6.94 | 2000 mm  [stored 6.56168 ft] | 1490 mm  [stored 4.88845 ft] | 2090 mm  [stored 6.85696 ft] | 0.555 | Yes | 1490 mm  [stored 4.88845 ft] | 0.518 | 5.24 | 0.584 | 6.76 | 1 mm  [stored 0.00328084 ft] | 1200 mm  [stored 3.93701 ft] | 300 mm  [stored 0.984252 ft] | 0.79 m² | 1410 mm | 711 mm | 711 mm | No | 2090 mm  [stored 6.85696 ft] | 2000 mm  [stored 6.56168 ft] |
| 540SW-2406XOX-1500Pa | 0.28 m² | 0.28 m² | 0.486 | 7.08 | 1500 mm  [stored 4.92126 ft] | 590 mm  [stored 1.9357 ft] | 2390 mm  [stored 7.84121 ft] | 0.437 | No | 590 mm  [stored 1.9357 ft] | 0.409 | 5.78 | 0.459 | 6.93 | 0 mm  [stored 0 ft] | 1200 mm  [stored 3.93701 ft] | 300 mm  [stored 0.984252 ft] | 0.28 m² | 510 mm | 811 mm | 811 mm | Yes | 2390 mm  [stored 7.84121 ft] | 1500 mm  [stored 4.92126 ft] |
| 540SW-2406XOX-2000Pa | 0.28 m² | 0.28 m² | 0.486 | 7.08 | 2000 mm  [stored 6.56168 ft] | 590 mm  [stored 1.9357 ft] | 2390 mm  [stored 7.84121 ft] | 0.437 | No | 590 mm  [stored 1.9357 ft] | 0.409 | 5.78 | 0.459 | 6.93 | 0 mm  [stored 0 ft] | 1200 mm  [stored 3.93701 ft] | 300 mm  [stored 0.984252 ft] | 0.28 m² | 510 mm | 811 mm | 811 mm | Yes | 2390 mm  [stored 7.84121 ft] | 2000 mm  [stored 6.56168 ft] |
| 540SW-2409XOX-1500Pa | 0.49 m² | 0.49 m² | 0.568 | 6.95 | 1500 mm  [stored 4.92126 ft] | 890 mm  [stored 2.91995 ft] | 2390 mm  [stored 7.84121 ft] | 0.51 | No | 890 mm  [stored 2.91995 ft] | 0.476 | 5.41 | 0.536 | 6.79 | 0 mm  [stored 0 ft] | 1200 mm  [stored 3.93701 ft] | 300 mm  [stored 0.984252 ft] | 0.49 m² | 810 mm  [stored 2.65748 ft] | 811 mm | 811 mm | Yes | 2390 mm  [stored 7.84121 ft] | 1500 mm  [stored 4.92126 ft] |
| 540SW-2409XOX-2000Pa | 0.49 m² | 0.49 m² | 0.568 | 6.95 | 2000 mm  [stored 6.56168 ft] | 890 mm  [stored 2.91995 ft] | 2390 mm  [stored 7.84121 ft] | 0.51 | No | 890 mm  [stored 2.91995 ft] | 0.476 | 5.41 | 0.536 | 6.79 | 0 mm  [stored 0 ft] | 1200 mm  [stored 3.93701 ft] | 300 mm  [stored 0.984252 ft] | 0.49 m² | 810 mm  [stored 2.65748 ft] | 811 mm | 811 mm | Yes | 2390 mm  [stored 7.84121 ft] | 2000 mm  [stored 6.56168 ft] |
| 540SW-2412XOX-1500Pa | 0.71 m² | 0.71 m² | 0.609 | 6.88 | 1500 mm  [stored 4.92126 ft] | 1190 mm  [stored 3.9042 ft] | 2390 mm  [stored 7.84121 ft] | 0.546 | No | 1190 mm  [stored 3.9042 ft] | 0.51 | 5.23 | 0.575 | 6.72 | 0 mm  [stored 0 ft] | 1200 mm  [stored 3.93701 ft] | 300 mm  [stored 0.984252 ft] | 0.71 m² | 1110 mm  [stored 3.64173 ft] | 811 mm | 811 mm | Yes | 2390 mm  [stored 7.84121 ft] | 1500 mm  [stored 4.92126 ft] |
| 540SW-2412XOX-2000Pa | 0.71 m² | 0.71 m² | 0.609 | 6.88 | 2000 mm  [stored 6.56168 ft] | 1190 mm  [stored 3.9042 ft] | 2390 mm  [stored 7.84121 ft] | 0.546 | Yes | 1190 mm  [stored 3.9042 ft] | 0.51 | 5.23 | 0.575 | 6.72 | 1 mm  [stored 0.00328084 ft] | 1200 mm  [stored 3.93701 ft] | 300 mm  [stored 0.984252 ft] | 0.71 m² | 1110 mm  [stored 3.64173 ft] | 811 mm | 811 mm | No | 2390 mm  [stored 7.84121 ft] | 2000 mm  [stored 6.56168 ft] |
| 540SW-2415XOX-1500Pa | 0.92 m² | 0.92 m² | 0.633 | 6.84 | 1500 mm  [stored 4.92126 ft] | 1490 mm  [stored 4.88845 ft] | 2390 mm  [stored 7.84121 ft] | 0.568 | Yes | 1490 mm  [stored 4.88845 ft] | 0.529 | 5.12 | 0.597 | 6.67 | 1 mm  [stored 0.00328084 ft] | 1200 mm  [stored 3.93701 ft] | 300 mm  [stored 0.984252 ft] | 0.92 m² | 1410 mm | 811 mm | 811 mm | No | 2390 mm  [stored 7.84121 ft] | 1500 mm  [stored 4.92126 ft] |
| 540SW-2415XOX-2000Pa | 0.92 m² | 0.92 m² | 0.633 | 6.84 | 2000 mm  [stored 6.56168 ft] | 1490 mm  [stored 4.88845 ft] | 2390 mm  [stored 7.84121 ft] | 0.568 | Yes | 1490 mm  [stored 4.88845 ft] | 0.529 | 5.12 | 0.597 | 6.67 | 1 mm  [stored 0.00328084 ft] | 1200 mm  [stored 3.93701 ft] | 300 mm  [stored 0.984252 ft] | 0.92 m² | 1410 mm | 811 mm | 811 mm | No | 2390 mm  [stored 7.84121 ft] | 2000 mm  [stored 6.56168 ft] |
| 540SW-2706XOX-1500Pa | 0.32 m² | 0.32 m² | 0.494 | 7.03 | 1500 mm  [stored 4.92126 ft] | 590 mm  [stored 1.9357 ft] | 2690 mm | 0.445 | No | 590 mm  [stored 1.9357 ft] | 0.416 | 5.71 | 0.467 | 6.88 | 0 mm  [stored 0 ft] | 1200 mm  [stored 3.93701 ft] | 334 mm | 0.32 m² | 510 mm | 911 mm | 911 mm | Yes | 2690 mm | 1500 mm  [stored 4.92126 ft] |
| 540SW-2706XOX-2000Pa | 0.32 m² | 0.32 m² | 0.494 | 7.03 | 2000 mm  [stored 6.56168 ft] | 590 mm  [stored 1.9357 ft] | 2690 mm | 0.445 | No | 590 mm  [stored 1.9357 ft] | 0.416 | 5.71 | 0.467 | 6.88 | 0 mm  [stored 0 ft] | 1200 mm  [stored 3.93701 ft] | 334 mm | 0.32 m² | 510 mm | 911 mm | 911 mm | Yes | 2690 mm | 2000 mm  [stored 6.56168 ft] |
| 540SW-2709XOX-1500Pa | 0.56 m² | 0.56 m² | 0.578 | 6.88 | 1500 mm  [stored 4.92126 ft] | 890 mm  [stored 2.91995 ft] | 2690 mm | 0.519 | No | 890 mm  [stored 2.91995 ft] | 0.484 | 5.32 | 0.546 | 6.72 | 0 mm  [stored 0 ft] | 1200 mm  [stored 3.93701 ft] | 334 mm | 0.56 m² | 810 mm  [stored 2.65748 ft] | 911 mm | 911 mm | Yes | 2690 mm | 1500 mm  [stored 4.92126 ft] |
| 540SW-2709XOX-2000Pa | 0.56 m² | 0.56 m² | 0.578 | 6.88 | 2000 mm  [stored 6.56168 ft] | 890 mm  [stored 2.91995 ft] | 2690 mm | 0.519 | No | 890 mm  [stored 2.91995 ft] | 0.484 | 5.32 | 0.546 | 6.72 | 0 mm  [stored 0 ft] | 1200 mm  [stored 3.93701 ft] | 334 mm | 0.56 m² | 810 mm  [stored 2.65748 ft] | 911 mm | 911 mm | Yes | 2690 mm | 2000 mm  [stored 6.56168 ft] |
| 540SW-2712XOX-1500Pa | 0.81 m² | 0.81 m² | 0.62 | 6.81 | 1500 mm  [stored 4.92126 ft] | 1190 mm  [stored 3.9042 ft] | 2690 mm | 0.556 | No | 1190 mm  [stored 3.9042 ft] | 0.518 | 5.13 | 0.585 | 6.65 | 0 mm  [stored 0 ft] | 1200 mm  [stored 3.93701 ft] | 334 mm | 0.81 m² | 1110 mm  [stored 3.64173 ft] | 911 mm | 911 mm | Yes | 2690 mm | 1500 mm  [stored 4.92126 ft] |
| 540SW-2712XOX-2000Pa | 0.81 m² | 0.81 m² | 0.62 | 6.81 | 2000 mm  [stored 6.56168 ft] | 1190 mm  [stored 3.9042 ft] | 2690 mm | 0.556 | Yes | 1190 mm  [stored 3.9042 ft] | 0.518 | 5.13 | 0.585 | 6.65 | 1 mm  [stored 0.00328084 ft] | 1200 mm  [stored 3.93701 ft] | 334 mm | 0.81 m² | 1110 mm  [stored 3.64173 ft] | 911 mm | 911 mm | No | 2690 mm | 2000 mm  [stored 6.56168 ft] |
| 540SW-2715XOX-1500Pa | 1.05 m² | 1.05 m² | 0.645 | 6.76 | 1500 mm  [stored 4.92126 ft] | 1490 mm  [stored 4.88845 ft] | 2690 mm | 0.578 | Yes | 1490 mm  [stored 4.88845 ft] | 0.539 | 5.02 | 0.608 | 6.6 | 1 mm  [stored 0.00328084 ft] | 1200 mm  [stored 3.93701 ft] | 334 mm | 1.05 m² | 1410 mm | 911 mm | 911 mm | No | 2690 mm | 1500 mm  [stored 4.92126 ft] |
| 540SW-2715XOX-2000Pa | 1.05 m² | 1.05 m² | 0.645 | 6.76 | 2000 mm  [stored 6.56168 ft] | 1490 mm  [stored 4.88845 ft] | 2690 mm | 0.578 | Yes | 1490 mm  [stored 4.88845 ft] | 0.539 | 5.02 | 0.608 | 6.6 | 1 mm  [stored 0.00328084 ft] | 1200 mm  [stored 3.93701 ft] | 334 mm | 1.05 m² | 1410 mm | 911 mm | 911 mm | No | 2690 mm | 2000 mm  [stored 6.56168 ft] |
| 540SW-3006XOX-1500Pa | 0.36 m² | 0.36 m² | 0.501 | 6.98 | 1500 mm  [stored 4.92126 ft] | 590 mm  [stored 1.9357 ft] | 2990 mm  [stored 9.80971 ft] | 0.45 | No | 590 mm  [stored 1.9357 ft] | 0.421 | 5.65 | 0.473 | 6.84 | 0 mm  [stored 0 ft] | 1200 mm  [stored 3.93701 ft] | 634 mm | 0.36 m² | 510 mm | 1011 mm | 1011 mm | Yes | 2990 mm  [stored 9.80971 ft] | 1500 mm  [stored 4.92126 ft] |
| 540SW-3006XOX-2000Pa | 0.36 m² | 0.36 m² | 0.501 | 6.98 | 2000 mm  [stored 6.56168 ft] | 590 mm  [stored 1.9357 ft] | 2990 mm  [stored 9.80971 ft] | 0.45 | No | 590 mm  [stored 1.9357 ft] | 0.421 | 5.65 | 0.473 | 6.84 | 0 mm  [stored 0 ft] | 1200 mm  [stored 3.93701 ft] | 634 mm | 0.36 m² | 510 mm | 1011 mm | 1011 mm | Yes | 2990 mm  [stored 9.80971 ft] | 2000 mm  [stored 6.56168 ft] |
| 540SW-3009XOX-1500Pa | 0.63 m² | 0.63 m² | 0.586 | 6.82 | 1500 mm  [stored 4.92126 ft] | 890 mm  [stored 2.91995 ft] | 2990 mm  [stored 9.80971 ft] | 0.526 | No | 890 mm  [stored 2.91995 ft] | 0.491 | 5.25 | 0.553 | 6.69 | 0 mm  [stored 0 ft] | 1200 mm  [stored 3.93701 ft] | 634 mm | 0.63 m² | 810 mm  [stored 2.65748 ft] | 1011 mm | 1011 mm | Yes | 2990 mm  [stored 9.80971 ft] | 1500 mm  [stored 4.92126 ft] |
| 540SW-3009XOX-2000Pa | 0.63 m² | 0.63 m² | 0.586 | 6.82 | 2000 mm  [stored 6.56168 ft] | 890 mm  [stored 2.91995 ft] | 2990 mm  [stored 9.80971 ft] | 0.526 | No | 890 mm  [stored 2.91995 ft] | 0.491 | 5.25 | 0.553 | 6.69 | 0 mm  [stored 0 ft] | 1200 mm  [stored 3.93701 ft] | 634 mm | 0.63 m² | 810 mm  [stored 2.65748 ft] | 1011 mm | 1011 mm | Yes | 2990 mm  [stored 9.80971 ft] | 2000 mm  [stored 6.56168 ft] |
| 540SW-3012XOX-1500Pa | 0.91 m² | 0.91 m² | 0.629 | 6.75 | 1500 mm  [stored 4.92126 ft] | 1190 mm  [stored 3.9042 ft] | 2990 mm  [stored 9.80971 ft] | 0.563 | No | 1190 mm  [stored 3.9042 ft] | 0.525 | 5.05 | 0.593 | 6.59 | 0 mm  [stored 0 ft] | 1200 mm  [stored 3.93701 ft] | 634 mm | 0.91 m² | 1110 mm  [stored 3.64173 ft] | 1011 mm | 1011 mm | Yes | 2990 mm  [stored 9.80971 ft] | 1500 mm  [stored 4.92126 ft] |
| 540SW-3012XOX-2000Pa | 0.91 m² | 0.91 m² | 0.629 | 6.75 | 2000 mm  [stored 6.56168 ft] | 1190 mm  [stored 3.9042 ft] | 2990 mm  [stored 9.80971 ft] | 0.563 | Yes | 1190 mm  [stored 3.9042 ft] | 0.525 | 5.05 | 0.593 | 6.59 | 1 mm  [stored 0.00328084 ft] | 1200 mm  [stored 3.93701 ft] | 634 mm | 0.91 m² | 1110 mm  [stored 3.64173 ft] | 1011 mm | 1011 mm | No | 2990 mm  [stored 9.80971 ft] | 2000 mm  [stored 6.56168 ft] |
| 540SW-3015XOX-1500Pa | 1.18 m² | 1.18 m² | 0.654 | 6.7 | 1500 mm  [stored 4.92126 ft] | 1490 mm  [stored 4.88845 ft] | 2990 mm  [stored 9.80971 ft] | 0.586 | Yes | 1490 mm  [stored 4.88845 ft] | 0.546 | 4.93 | 0.617 | 6.54 | 1 mm  [stored 0.00328084 ft] | 1200 mm  [stored 3.93701 ft] | 634 mm | 1.18 m² | 1410 mm | 1011 mm | 1011 mm | No | 2990 mm  [stored 9.80971 ft] | 1500 mm  [stored 4.92126 ft] |
| 540SW-3015XOX-2000Pa | 1.18 m² | 1.18 m² | 0.654 | 6.7 | 2000 mm  [stored 6.56168 ft] | 1490 mm  [stored 4.88845 ft] | 2990 mm  [stored 9.80971 ft] | 0.586 | Yes | 1490 mm  [stored 4.88845 ft] | 0.546 | 4.93 | 0.617 | 6.54 | 1 mm  [stored 0.00328084 ft] | 1200 mm  [stored 3.93701 ft] | 634 mm | 1.18 m² | 1410 mm | 1011 mm | 1011 mm | No | 2990 mm  [stored 9.80971 ft] | 2000 mm  [stored 6.56168 ft] |

note: [stored X ft] marks values corroborated as IEEE doubles in the binary element streams (Revit-internal decimal feet)

## geometry (parser evidence)
native form markers: Sweep x8
no freeform markers — native parametric forms only
